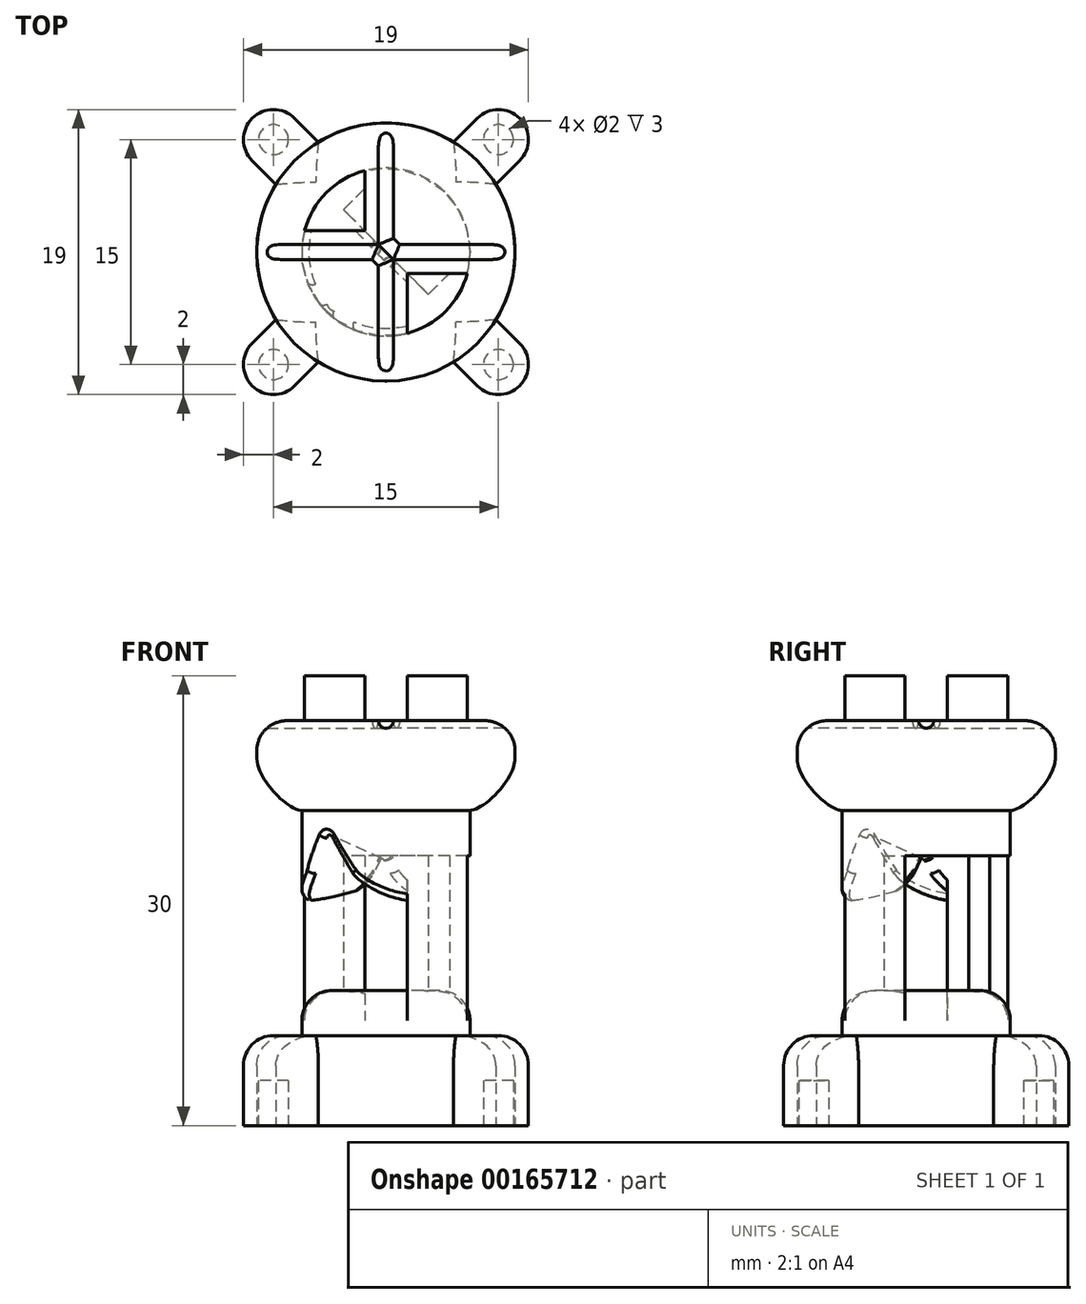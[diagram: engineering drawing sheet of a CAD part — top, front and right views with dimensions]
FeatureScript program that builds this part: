
annotation { "Feature Type Name" : "Feature", "Feature Type Description" : "" }
export const myFeature = defineFeature(function(context is Context, id is Id, definition is map)
    precondition{}
    {
        {
            assignVariable(context, id + "F0", {"name" : "squareSize", "anyValue" : 25 * mm});
        }
        {
            assignVariable(context, id + "F1", {"name" : "magnetHeight", "anyValue" : 3 * mm});
        }
        {
            assignVariable(context, id + "F2", {"name" : "thickness", "anyValue" : 3 * mm});
        }
        {
            var Q0;
            Q0=qCreatedBy(makeId("Top.planeOp"),FACE);
            var sketch = newSketch(context, id + "F3", { "sketchPlane" : qUnion([Q0])});
            skLineSegment(sketch, "E0.bottom", {"start": v(0, 0) * mm, "end": v(25, 0) * mm});
            skLineSegment(sketch, "E0.top", {"start": v(0, 25) * mm, "end": v(25, 25) * mm});
            skLineSegment(sketch, "E0.left", {"start": v(0, 0) * mm, "end": v(0, 25) * mm});
            skLineSegment(sketch, "E0.right", {"start": v(25, 0) * mm, "end": v(25, 25) * mm});
            skLineSegment(sketch, "E1", {"start": v(0, 0) * mm, "end": v(5, 0) * mm, "construction": true});
            skLineSegment(sketch, "E2", {"start": v(5, 0) * mm, "end": v(20, 0) * mm, "construction": true});
            skLineSegment(sketch, "E3", {"start": v(20, 0) * mm, "end": v(25, 0) * mm, "construction": true});
            skLineSegment(sketch, "E4", {"start": v(0, 0) * mm, "end": v(0, 5) * mm, "construction": true});
            skLineSegment(sketch, "E5", {"start": v(0, 5) * mm, "end": v(0, 20) * mm, "construction": true});
            skLineSegment(sketch, "E6", {"start": v(0, 20) * mm, "end": v(0, 25) * mm, "construction": true});
            skPoint(sketch, "E7", {"position": v(5, 5) * mm});
            skPoint(sketch, "E8", {"position": v(20, 5) * mm});
            skPoint(sketch, "E9", {"position": v(5, 20) * mm});
            skPoint(sketch, "E10", {"position": v(20, 20) * mm});
            skCircle(sketch, "E11", {"center": v(5, 20) * mm, "radius": 1 * mm});
            skCircle(sketch, "E12", {"center": v(20, 20) * mm, "radius": 1 * mm});
            skCircle(sketch, "E13", {"center": v(20, 5) * mm, "radius": 1 * mm});
            skCircle(sketch, "E14", {"center": v(5, 5) * mm, "radius": 1 * mm});
            skCircle(sketch, "E15", {"center": v(5, 20) * mm, "radius": 2 * mm});
            skCircle(sketch, "E16", {"center": v(20, 20) * mm, "radius": 2 * mm});
            skCircle(sketch, "E17", {"center": v(20, 5) * mm, "radius": 2 * mm});
            skCircle(sketch, "E18", {"center": v(5, 5) * mm, "radius": 2 * mm});
            skLineSegment(sketch, "E19", {"start": v(3.59, 18.59) * mm, "end": v(18.59, 3.59) * mm, "construction": true});
            skLineSegment(sketch, "E20", {"start": v(21.41, 6.41) * mm, "end": v(6.41, 21.41) * mm, "construction": true});
            skLineSegment(sketch, "E21", {"start": v(18.59, 21.41) * mm, "end": v(3.59, 6.41) * mm, "construction": true});
            skLineSegment(sketch, "E22", {"start": v(6.41, 3.59) * mm, "end": v(21.41, 18.59) * mm, "construction": true});
            skCircle(sketch, "E23", {"center": v(12.5, 12.5) * mm, "radius": 8.6 * mm});
            skPoint(sketch, "E23.centerSnap0", {"position": v(12.5, 0) * mm});
            skPoint(sketch, "E23.centerSnap1", {"position": v(0, 12.5) * mm});
            skLineSegment(sketch, "E24", {"start": v(18.59, 21.41) * mm, "end": v(17, 19.83) * mm});
            skLineSegment(sketch, "E25", {"start": v(21.41, 18.59) * mm, "end": v(19.83, 17) * mm});
            skLineSegment(sketch, "E26", {"start": v(21.41, 6.41) * mm, "end": v(19.83, 8) * mm});
            skLineSegment(sketch, "E27", {"start": v(18.59, 3.59) * mm, "end": v(17, 5.17) * mm});
            skLineSegment(sketch, "E28", {"start": v(3.59, 6.41) * mm, "end": v(5.17, 8) * mm});
            skLineSegment(sketch, "E29", {"start": v(6.41, 3.59) * mm, "end": v(8, 5.17) * mm});
            skLineSegment(sketch, "E30", {"start": v(3.59, 18.59) * mm, "end": v(5.17, 17) * mm});
            skLineSegment(sketch, "E31", {"start": v(6.41, 21.41) * mm, "end": v(8, 19.83) * mm});
            skCircle(sketch, "E32.0", {"center": v(12.5, 12.5) * mm, "radius": 5.6 * mm});
            skLineSegment(sketch, "E33", {"start": v(11.09, 13.91) * mm, "end": v(7.07, 13.91) * mm});
            skLineSegment(sketch, "E34", {"start": v(13.91, 11.09) * mm, "end": v(13.91, 7.07) * mm});
            skLineSegment(sketch, "E35", {"start": v(5, 20) * mm, "end": v(20, 5) * mm, "construction": true});
            skLineSegment(sketch, "E36", {"start": v(11.09, 17.93) * mm, "end": v(11.09, 16.74) * mm});
            skLineSegment(sketch, "E37", {"start": v(11.09, 16.74) * mm, "end": v(9.67, 15.33) * mm});
            skLineSegment(sketch, "E38", {"start": v(17.93, 11.09) * mm, "end": v(16.74, 11.09) * mm});
            skLineSegment(sketch, "E39", {"start": v(16.74, 11.09) * mm, "end": v(15.33, 9.67) * mm});
            skLineSegment(sketch, "E40", {"start": v(15.33, 9.67) * mm, "end": v(13.91, 11.09) * mm});
            skLineSegment(sketch, "E41", {"start": v(13.91, 11.09) * mm, "end": v(11.09, 13.91) * mm});
            skLineSegment(sketch, "E42", {"start": v(9.67, 15.33) * mm, "end": v(11.09, 13.91) * mm});
            skLineSegment(sketch, "E43", {"start": v(11.09, 13.91) * mm, "end": v(11.09, 16.74) * mm});
            skLineSegment(sketch, "E44", {"start": v(13.91, 11.09) * mm, "end": v(16.74, 11.09) * mm});
            skSolve(sketch);
        }
        {
            var Q0;
            Q0=makeQuery(id+"F3.imprint","IMPRINT",FACE,{"disambiguationData":[TD([[makeQuery(id+"F3.imprint","IMPRINT",EDGE,{"derivedFrom":sQuery(id+"F3.wireOp",EDGE,"E37")}),1.0]])]});
            var Q1;
            {var subQ1=sQuery(id+"F3.wireOp",EDGE,"E36");Q1=makeQuery(id+"F3.imprint","IMPRINT",FACE,{"disambiguationData":[TD([[makeQuery(id+"F3.imprint","IMPRINT",EDGE,{"derivedFrom":subQ1}),1.0]])]});}
            var Q2;
            {var subQ1=sQuery(id+"F3.wireOp",EDGE,"E33");Q2=makeQuery(id+"F3.imprint","IMPRINT",FACE,{"disambiguationData":[TD([[makeQuery(id+"F3.imprint","IMPRINT",EDGE,{"derivedFrom":subQ1}),-1.0]])]});}
            var Q3;
            {var subQ0=sQuery(id+"F3.wireOp",EDGE,"E34");Q3=makeQuery(id+"F3.imprint","IMPRINT",FACE,{"disambiguationData":[TD([[makeQuery(id+"F3.imprint","IMPRINT",EDGE,{"derivedFrom":subQ0}),1.0]])]});}
            var Q4;
            Q4=makeQuery(id+"F3.imprint","IMPRINT",FACE,{"disambiguationData":[TD([[makeQuery(id+"F3.imprint","IMPRINT",EDGE,{"derivedFrom":sQuery(id+"F3.wireOp",EDGE,"E39")}),-1.0]])]});
            var Q5;
            {var subQ0=sQuery(id+"F3.wireOp",EDGE,"E33");Q5=makeQuery(id+"F3.imprint","IMPRINT",FACE,{"disambiguationData":[TD([[makeQuery(id+"F3.imprint","IMPRINT",EDGE,{"derivedFrom":subQ0}),1.0]])]});}
            var Q6;
            {var subQ0=sQuery(id+"F3.wireOp",EDGE,"E23");var subQ11=makeQuery(id+"F3.imprint","INTERSECT",VERTEX,{"derivedFrom":[subQ0,sQuery(id+"F3.wireOp",EDGE,"E25")]});Q6=makeQuery(id+"F3.imprint","IMPRINT",FACE,{"disambiguationData":[TD([[makeQuery(id+"F3.imprint","IMPRINT",EDGE,{"disambiguationData":[TD([[subQ11,-1.0]])],"derivedFrom":subQ0}),1.0]])]});}
            var Q7;
            {var subQ0=sQuery(id+"F3.wireOp",EDGE,"E25");Q7=makeQuery(id+"F3.imprint","IMPRINT",FACE,{"disambiguationData":[TD([[makeQuery(id+"F3.imprint","IMPRINT",EDGE,{"derivedFrom":subQ0}),-1.0]])]});}
            var Q8;
            Q8=makeQuery(id+"F3.imprint","IMPRINT",FACE,{"disambiguationData":[TD([[makeQuery(id+"F3.imprint","IMPRINT",EDGE,{"derivedFrom":sQuery(id+"F3.wireOp",EDGE,"E12")}),-1.0]])]});
            var Q9;
            {var subQ0=sQuery(id+"F3.wireOp",EDGE,"E24");Q9=makeQuery(id+"F3.imprint","IMPRINT",FACE,{"disambiguationData":[TD([[makeQuery(id+"F3.imprint","IMPRINT",EDGE,{"derivedFrom":subQ0}),1.0]])]});}
            var Q10;
            {var subQ0=sQuery(id+"F3.wireOp",EDGE,"E30");Q10=makeQuery(id+"F3.imprint","IMPRINT",FACE,{"disambiguationData":[TD([[makeQuery(id+"F3.imprint","IMPRINT",EDGE,{"derivedFrom":subQ0}),1.0]])]});}
            var Q11;
            Q11=makeQuery(id+"F3.imprint","IMPRINT",FACE,{"disambiguationData":[TD([[makeQuery(id+"F3.imprint","IMPRINT",EDGE,{"derivedFrom":sQuery(id+"F3.wireOp",EDGE,"E11")}),-1.0]])]});
            var Q12;
            {var subQ0=sQuery(id+"F3.wireOp",EDGE,"E31");Q12=makeQuery(id+"F3.imprint","IMPRINT",FACE,{"disambiguationData":[TD([[makeQuery(id+"F3.imprint","IMPRINT",EDGE,{"derivedFrom":subQ0}),-1.0]])]});}
            var Q13;
            Q13=makeQuery(id+"F3.imprint","IMPRINT",FACE,{"disambiguationData":[TD([[makeQuery(id+"F3.imprint","IMPRINT",EDGE,{"derivedFrom":sQuery(id+"F3.wireOp",EDGE,"E14")}),-1.0]])]});
            var Q14;
            {var subQ0=sQuery(id+"F3.wireOp",EDGE,"E28");Q14=makeQuery(id+"F3.imprint","IMPRINT",FACE,{"disambiguationData":[TD([[makeQuery(id+"F3.imprint","IMPRINT",EDGE,{"derivedFrom":subQ0}),-1.0]])]});}
            var Q15;
            {var subQ0=sQuery(id+"F3.wireOp",EDGE,"E29");Q15=makeQuery(id+"F3.imprint","IMPRINT",FACE,{"disambiguationData":[TD([[makeQuery(id+"F3.imprint","IMPRINT",EDGE,{"derivedFrom":subQ0}),1.0]])]});}
            var Q16;
            {var subQ0=sQuery(id+"F3.wireOp",EDGE,"E27");Q16=makeQuery(id+"F3.imprint","IMPRINT",FACE,{"disambiguationData":[TD([[makeQuery(id+"F3.imprint","IMPRINT",EDGE,{"derivedFrom":subQ0}),-1.0]])]});}
            var Q17;
            Q17=makeQuery(id+"F3.imprint","IMPRINT",FACE,{"disambiguationData":[TD([[makeQuery(id+"F3.imprint","IMPRINT",EDGE,{"derivedFrom":sQuery(id+"F3.wireOp",EDGE,"E13")}),-1.0]])]});
            var Q18;
            {var subQ0=sQuery(id+"F3.wireOp",EDGE,"E26");Q18=makeQuery(id+"F3.imprint","IMPRINT",FACE,{"disambiguationData":[TD([[makeQuery(id+"F3.imprint","IMPRINT",EDGE,{"derivedFrom":subQ0}),1.0]])]});}
            var Q19;
            Q19=makeQuery(id+"FElZrmsSUFFGGNs_0.opExtrude","SWEPT_FACE",FACE,{"disambiguationData":[OSD([sQuery(id+"FqHbGi2moSqKO1t.wireOp",EDGE,"XD9OQdDl-AIoh-yf8k-eY9A-MIdfoNcweXZ7")])]});
            extrude(context, id + "F4", {"entities" : qUnion([Q0, Q1, Q2, Q3, Q4, Q5, Q6, Q7, Q8, Q9, Q10, Q11, Q12, Q13, Q14, Q15, Q16, Q17, Q18]), "endBoundEntityFace" : qUnion([Q19]), "depth" : getVariable(context, 'magnetHeight')});
        }
        {
            var Q0;
            Q0=makeQuery(id+"F4.opExtrude","CAP_FACE",FACE,{"disambiguationData":[OSD([sQuery(id+"F3.wireOp",EDGE,"E11"),sQuery(id+"F3.wireOp",EDGE,"E12"),sQuery(id+"F3.wireOp",EDGE,"E13"),sQuery(id+"F3.wireOp",EDGE,"E14"),sQuery(id+"F3.wireOp",EDGE,"E15"),sQuery(id+"F3.wireOp",EDGE,"E16"),sQuery(id+"F3.wireOp",EDGE,"E17"),sQuery(id+"F3.wireOp",EDGE,"E18"),sQuery(id+"F3.wireOp",EDGE,"E23"),sQuery(id+"F3.wireOp",EDGE,"E24"),sQuery(id+"F3.wireOp",EDGE,"E25"),sQuery(id+"F3.wireOp",EDGE,"E26"),sQuery(id+"F3.wireOp",EDGE,"E27"),sQuery(id+"F3.wireOp",EDGE,"E28"),sQuery(id+"F3.wireOp",EDGE,"E29"),sQuery(id+"F3.wireOp",EDGE,"E30"),sQuery(id+"F3.wireOp",EDGE,"E31")])],"isStart":false});
            var sketch = newSketch(context, id + "F5", { "sketchPlane" : qUnion([Q0])});
            skLineSegment(sketch, "E45.0", {"start": v(3.59, 18.59) * mm, "end": v(5.17, 17) * mm});
            skCircle(sketch, "E45.1", {"center": v(12.5, 12.5) * mm, "radius": 8.6 * mm});
            skCircle(sketch, "E45.2", {"center": v(5, 20) * mm, "radius": 2 * mm});
            skLineSegment(sketch, "E45.3", {"start": v(6.41, 21.41) * mm, "end": v(8, 19.83) * mm});
            skLineSegment(sketch, "E45.4", {"start": v(18.59, 21.41) * mm, "end": v(17, 19.83) * mm});
            skCircle(sketch, "E45.5", {"center": v(20, 20) * mm, "radius": 2 * mm});
            skLineSegment(sketch, "E45.6", {"start": v(21.41, 18.59) * mm, "end": v(19.83, 17) * mm});
            skLineSegment(sketch, "E45.7", {"start": v(21.41, 6.41) * mm, "end": v(19.83, 8) * mm});
            skCircle(sketch, "E46.0", {"center": v(20, 5) * mm, "radius": 2 * mm});
            skLineSegment(sketch, "E46.1", {"start": v(18.59, 3.59) * mm, "end": v(17, 5.17) * mm});
            skLineSegment(sketch, "E46.2", {"start": v(6.41, 3.59) * mm, "end": v(8, 5.17) * mm});
            skCircle(sketch, "E46.3", {"center": v(5, 5) * mm, "radius": 2 * mm});
            skLineSegment(sketch, "E47.0", {"start": v(3.59, 6.41) * mm, "end": v(5.17, 8) * mm});
            skSolve(sketch);
        }
        {
            var Q0;
            Q0 = qSketchRegion(id + "F5", true);
            var Q1;
            Q1=makeQuery(id+"FElZrmsSUFFGGNs_0.opExtrude","SWEPT_FACE",FACE,{"disambiguationData":[OSD([sQuery(id+"FqHbGi2moSqKO1t.wireOp",EDGE,"9eabc2cb-ff13-4b68-a3ec-a71c30de9d8a")])]});
            var Q2;
            Q2=makeQuery(id+"FElZrmsSUFFGGNs_0.opExtrude","SWEPT_FACE",FACE,{"disambiguationData":[OSD([sQuery(id+"FqHbGi2moSqKO1t.wireOp",EDGE,"XD9OQdDl-AIoh-yf8k-eY9A-MIdfoNcweXZ7")])]});
            extrude(context, id + "F6", {"entities" : qUnion([Q0]), "operationType" : NewBodyOperationType.ADD, "endBoundEntityFace" : qUnion([Q1]), "depth" : getVariable(context, 'thickness')});
        }
        {
            var Q0;
            Q0=makeQuery(id+"F6.opExtrude","CAP_FACE",FACE,{"disambiguationData":[OSD([sQuery(id+"F5.wireOp",EDGE,"E45.0"),sQuery(id+"F5.wireOp",EDGE,"E45.1"),sQuery(id+"F5.wireOp",EDGE,"E45.2"),sQuery(id+"F5.wireOp",EDGE,"E45.3"),sQuery(id+"F5.wireOp",EDGE,"E45.4"),sQuery(id+"F5.wireOp",EDGE,"E45.5"),sQuery(id+"F5.wireOp",EDGE,"E45.6"),sQuery(id+"F5.wireOp",EDGE,"E45.7"),sQuery(id+"F5.wireOp",EDGE,"E46.0"),sQuery(id+"F5.wireOp",EDGE,"E46.1"),sQuery(id+"F5.wireOp",EDGE,"E46.2"),sQuery(id+"F5.wireOp",EDGE,"E46.3"),sQuery(id+"F5.wireOp",EDGE,"E47.0")])],"isStart":false});
            var sketch = newSketch(context, id + "F7", { "sketchPlane" : qUnion([Q0])});
            skCircle(sketch, "E48.0", {"center": v(12.5, 12.5) * mm, "radius": 5.6 * mm});
            skSolve(sketch);
        }
        {
            var Q0;
            Q0 = qSketchRegion(id + "F7", true);
            var Q1;
            Q1=makeQuery(id+"FElZrmsSUFFGGNs_0.opExtrude","SWEPT_FACE",FACE,{"disambiguationData":[OSD([sQuery(id+"FqHbGi2moSqKO1t.wireOp",EDGE,"AaM88Yrc-j56C-Fqkk-HDkq-REDH0FS8FcKS")])]});
            var Q2;
            Q2=makeQuery(id+"FElZrmsSUFFGGNs_0.opExtrude","SWEPT_FACE",FACE,{"disambiguationData":[OSD([sQuery(id+"FqHbGi2moSqKO1t.wireOp",EDGE,"9eabc2cb-ff13-4b68-a3ec-a71c30de9d8a")])]});
            extrude(context, id + "F8", {"entities" : qUnion([Q0]), "operationType" : NewBodyOperationType.ADD, "endBoundEntityFace" : qUnion([Q1]), "depth" : getVariable(context, 'thickness')});
        }
        {
            var Q0;
            Q0=makeQuery(id+"F8.opExtrude","CAP_FACE",FACE,{"disambiguationData":[OSD([sQuery(id+"F7.wireOp",EDGE,"E48.0")])],"isStart":false});
            var sketch = newSketch(context, id + "F9", { "sketchPlane" : qUnion([Q0])});
            skLineSegment(sketch, "E49.0", {"start": v(11.09, 13.91) * mm, "end": v(7.07, 13.91) * mm});
            skLineSegment(sketch, "E49.1", {"start": v(9.67, 15.33) * mm, "end": v(11.09, 13.91) * mm});
            skLineSegment(sketch, "E49.2", {"start": v(11.09, 16.74) * mm, "end": v(9.67, 15.33) * mm});
            skCircle(sketch, "E49.3", {"center": v(12.5, 12.5) * mm, "radius": 5.6 * mm});
            skLineSegment(sketch, "E49.4", {"start": v(15.33, 9.67) * mm, "end": v(13.91, 11.09) * mm});
            skLineSegment(sketch, "E49.5", {"start": v(16.74, 11.09) * mm, "end": v(15.33, 9.67) * mm});
            skLineSegment(sketch, "E49.6", {"start": v(17.93, 11.09) * mm, "end": v(16.74, 11.09) * mm});
            skLineSegment(sketch, "E49.7", {"start": v(11.09, 17.93) * mm, "end": v(11.09, 16.74) * mm});
            skLineSegment(sketch, "E49.8", {"start": v(13.91, 11.09) * mm, "end": v(13.91, 7.07) * mm});
            skSolve(sketch);
        }
        {
            var Q0;
            {var subQ1=sQuery(id+"F9.wireOp",EDGE,"E49.0");Q0=makeQuery(id+"F9.imprint","IMPRINT",FACE,{"disambiguationData":[TD([[makeQuery(id+"F9.imprint","IMPRINT",EDGE,{"derivedFrom":subQ1}),-1.0]])]});}
            var Q1;
            Q1=makeQuery(id+"F9.imprint","IMPRINT",FACE,{"disambiguationData":[TD([[makeQuery(id+"F9.imprint","IMPRINT",EDGE,{"derivedFrom":sQuery(id+"F9.wireOp",EDGE,"E49.4")}),1.0]])]});
            var Q2;
            Q2=makeQuery(id+"FElZrmsSUFFGGNs_0.opExtrude","SWEPT_FACE",FACE,{"disambiguationData":[OSD([sQuery(id+"FqHbGi2moSqKO1t.wireOp",EDGE,"z7yksMqY-2ZQH-XZhy-clyX-XMTxwlro2wc1")])]});
            var Q3;
            Q3=makeQuery(id+"FElZrmsSUFFGGNs_0.opExtrude","SWEPT_FACE",FACE,{"disambiguationData":[OSD([sQuery(id+"FqHbGi2moSqKO1t.wireOp",EDGE,"AaM88Yrc-j56C-Fqkk-HDkq-REDH0FS8FcKS")])]});
            extrude(context, id + "F10", {"entities" : qUnion([Q0, Q1]), "operationType" : NewBodyOperationType.ADD, "endBoundEntityFace" : qUnion([Q2]), "depth" : 2 * getVariable(context, 'thickness')});
        }
        {
            var Q0;
            Q0=makeQuery(id+"F10.opExtrude","CAP_FACE",FACE,{"disambiguationData":[OSD([sQuery(id+"F9.wireOp",EDGE,"E49.3"),sQuery(id+"F9.wireOp",EDGE,"E49.4"),sQuery(id+"F9.wireOp",EDGE,"E49.5"),sQuery(id+"F9.wireOp",EDGE,"E49.6"),sQuery(id+"F9.wireOp",EDGE,"E49.8")])],"isStart":false});
            var sketch = newSketch(context, id + "F11", { "sketchPlane" : qUnion([Q0])});
            skLineSegment(sketch, "E50.0", {"start": v(15.33, 9.67) * mm, "end": v(13.91, 11.09) * mm});
            skLineSegment(sketch, "E50.1", {"start": v(16.74, 11.09) * mm, "end": v(15.33, 9.67) * mm});
            skLineSegment(sketch, "E50.2", {"start": v(17.93, 11.09) * mm, "end": v(16.74, 11.09) * mm});
            skCircle(sketch, "E50.3", {"center": v(12.5, 12.5) * mm, "radius": 5.6 * mm});
            skLineSegment(sketch, "E51.0", {"start": v(9.67, 15.33) * mm, "end": v(11.09, 13.91) * mm});
            skLineSegment(sketch, "E51.1", {"start": v(11.09, 16.74) * mm, "end": v(9.67, 15.33) * mm});
            skLineSegment(sketch, "E51.2", {"start": v(11.09, 17.93) * mm, "end": v(11.09, 16.74) * mm});
            skLineSegment(sketch, "E52", {"start": v(11.09, 13.91) * mm, "end": v(13.91, 11.09) * mm});
            skSolve(sketch);
        }
        {
            var Q0;
            Q0=makeQuery(id+"F11.imprint","IMPRINT",FACE,{"disambiguationData":[TD([[makeQuery(id+"F11.imprint","IMPRINT",EDGE,{"derivedFrom":sQuery(id+"F11.wireOp",EDGE,"E50.0")}),1.0]])]});
            var Q1;
            Q1=makeQuery(id+"F11.imprint","IMPRINT",FACE,{"disambiguationData":[TD([[makeQuery(id+"F11.imprint","IMPRINT",EDGE,{"derivedFrom":sQuery(id+"F11.wireOp",EDGE,"E51.0")}),-1.0]])]});
            extrude(context, id + "F12", {"entities" : qUnion([Q0, Q1]), "operationType" : NewBodyOperationType.ADD, "depth" : getVariable(context, 'thickness')});
        }
        {
            var Q0;
            Q0=makeQuery(id+"F12.opExtrude","CAP_FACE",FACE,{"disambiguationData":[OSD([sQuery(id+"F11.wireOp",EDGE,"E50.0"),sQuery(id+"F11.wireOp",EDGE,"E50.1"),sQuery(id+"F11.wireOp",EDGE,"E50.2"),sQuery(id+"F11.wireOp",EDGE,"E50.3"),sQuery(id+"F11.wireOp",EDGE,"E51.0"),sQuery(id+"F11.wireOp",EDGE,"E51.1"),sQuery(id+"F11.wireOp",EDGE,"E51.2"),sQuery(id+"F11.wireOp",EDGE,"E52")])],"isStart":false});
            var sketch = newSketch(context, id + "F13", { "sketchPlane" : qUnion([Q0])});
            skCircle(sketch, "E53.0", {"center": v(12.5, 12.5) * mm, "radius": 5.6 * mm});
            skSolve(sketch);
        }
        {
            var Q0;
            Q0=makeQuery(id+"F13.imprint","IMPRINT",FACE,{"disambiguationData":[TD([[makeQuery(id+"F13.imprint","IMPRINT",EDGE,{"derivedFrom":makeQuery(id+"F12.opExtrude","CAP_EDGE",EDGE,{"disambiguationData":[OSD([sQuery(id+"F11.wireOp",EDGE,"E50.1")])],"isStart":false})}),1.0]])]});
            var Q1;
            Q1=makeQuery(id+"F13.imprint","IMPRINT",FACE,{"disambiguationData":[TD([[makeQuery(id+"F13.imprint","IMPRINT",EDGE,{"derivedFrom":makeQuery(id+"F12.opExtrude","CAP_EDGE",EDGE,{"disambiguationData":[OSD([sQuery(id+"F11.wireOp",EDGE,"E50.1")])],"isStart":false})}),-1.0]])]});
            var Q2;
            Q2=makeQuery(id+"FElZrmsSUFFGGNs_0.opExtrude","SWEPT_FACE",FACE,{"disambiguationData":[OSD([sQuery(id+"FqHbGi2moSqKO1t.wireOp",EDGE,"eM3HZQxG-NVRT-AnBt-5DXk-xiImXyo5NWNo")])]});
            var Q3;
            Q3=makeQuery(id+"FElZrmsSUFFGGNs_0.opExtrude","SWEPT_FACE",FACE,{"disambiguationData":[OSD([sQuery(id+"FqHbGi2moSqKO1t.wireOp",EDGE,"z7yksMqY-2ZQH-XZhy-clyX-XMTxwlro2wc1")])]});
            extrude(context, id + "F14", {"entities" : qUnion([Q0, Q1]), "operationType" : NewBodyOperationType.ADD, "endBoundEntityFace" : qUnion([Q2]), "depth" : getVariable(context, 'thickness')});
        }
        {
            var Q0;
            Q0=makeQuery(id+"F14.opExtrude","CAP_FACE",FACE,{"disambiguationData":[OSD([sQuery(id+"F13.wireOp",EDGE,"E53.0")])],"isStart":false});
            var sketch = newSketch(context, id + "F15", { "sketchPlane" : qUnion([Q0])});
            skCircle(sketch, "E54.0", {"center": v(12.5, 12.5) * mm, "radius": 8.6 * mm});
            skSolve(sketch);
        }
        {
            var Q0;
            Q0 = qSketchRegion(id + "F15", true);
            var Q1;
            Q1=makeQuery(id+"FElZrmsSUFFGGNs_0.opExtrude","SWEPT_FACE",FACE,{"disambiguationData":[OSD([sQuery(id+"FqHbGi2moSqKO1t.wireOp",EDGE,"O0l0VlI1-JJUv-K6Yr-c7LZ-AkOMDPOYUOIM")])]});
            var Q2;
            Q2=makeQuery(id+"FElZrmsSUFFGGNs_0.opExtrude","SWEPT_FACE",FACE,{"disambiguationData":[OSD([sQuery(id+"FqHbGi2moSqKO1t.wireOp",EDGE,"eM3HZQxG-NVRT-AnBt-5DXk-xiImXyo5NWNo")])]});
            extrude(context, id + "F16", {"entities" : qUnion([Q0]), "operationType" : NewBodyOperationType.ADD, "endBoundEntityFace" : qUnion([Q1]), "depth" : 2 * getVariable(context, 'thickness')});
        }
        {
            var Q0;
            Q0=makeQuery(id+"F16.opExtrude","CAP_FACE",FACE,{"disambiguationData":[OSD([sQuery(id+"F15.wireOp",EDGE,"E54.0")])],"isStart":false});
            var sketch = newSketch(context, id + "F17", { "sketchPlane" : qUnion([Q0])});
            skLineSegment(sketch, "E55.0", {"start": v(11.09, 13.91) * mm, "end": v(7.07, 13.91) * mm});
            skCircle(sketch, "E55.1", {"center": v(12.5, 12.5) * mm, "radius": 5.6 * mm});
            skLineSegment(sketch, "E55.4", {"start": v(11.09, 17.93) * mm, "end": v(11.09, 16.74) * mm});
            skLineSegment(sketch, "E55.5", {"start": v(13.91, 11.09) * mm, "end": v(13.91, 7.07) * mm});
            skLineSegment(sketch, "E55.8", {"start": v(17.93, 11.09) * mm, "end": v(16.74, 11.09) * mm});
            skLineSegment(sketch, "E56.0", {"start": v(13.91, 11.09) * mm, "end": v(16.74, 11.09) * mm});
            skLineSegment(sketch, "E56.1", {"start": v(11.09, 13.91) * mm, "end": v(11.09, 16.74) * mm});
            skSolve(sketch);
        }
        {
            var Q0;
            {var subQ0=sQuery(id+"F17.wireOp",EDGE,"E55.0");Q0=makeQuery(id+"F17.imprint","IMPRINT",FACE,{"disambiguationData":[TD([[makeQuery(id+"F17.imprint","IMPRINT",EDGE,{"derivedFrom":subQ0}),-1.0]])]});}
            var Q1;
            {var subQ0=sQuery(id+"F17.wireOp",EDGE,"E55.5");Q1=makeQuery(id+"F17.imprint","IMPRINT",FACE,{"disambiguationData":[TD([[makeQuery(id+"F17.imprint","IMPRINT",EDGE,{"derivedFrom":subQ0}),1.0]])]});}
            var Q2;
            Q2=makeQuery(id+"FElZrmsSUFFGGNs_0.opExtrude","SWEPT_FACE",FACE,{"disambiguationData":[OSD([sQuery(id+"FqHbGi2moSqKO1t.wireOp",EDGE,"O0l0VlI1-JJUv-K6Yr-c7LZ-AkOMDPOYUOIM")])]});
            extrude(context, id + "F18", {"entities" : qUnion([Q0, Q1]), "operationType" : NewBodyOperationType.ADD, "depth" : getVariable(context, 'thickness')});
        }
        {
            var Q0;
            Q0=makeQuery(id+"F12.boolean.opBoolean","MERGE",FACE,{"derivedFrom":[makeQuery(id+"F10.opExtrude","SWEPT_FACE",FACE,{"disambiguationData":[OSD([sQuery(id+"F9.wireOp",EDGE,"E49.1")])]}),makeQuery(id+"F10.opExtrude","SWEPT_FACE",FACE,{"disambiguationData":[OSD([sQuery(id+"F9.wireOp",EDGE,"E49.4")])]}),makeQuery(id+"F12.opExtrude","SWEPT_FACE",FACE,{"disambiguationData":[OSD([sQuery(id+"F11.wireOp",EDGE,"E50.0"),sQuery(id+"F11.wireOp",EDGE,"E51.0"),sQuery(id+"F11.wireOp",EDGE,"E52")])]})]});
            var sketch = newSketch(context, id + "F19", { "sketchPlane" : qUnion([Q0])});
            skLineSegment(sketch, "E57.0", {"start": v(-2, 15) * mm, "end": v(2, 15) * mm});
            skLineSegment(sketch, "E57.1", {"start": v(-4, 18) * mm, "end": v(4, 18) * mm});
            skLineSegment(sketch, "E58", {"start": v(2, 15) * mm, "end": v(0, 18) * mm});
            skLineSegment(sketch, "E59", {"start": v(-2, 15) * mm, "end": v(0, 18) * mm});
            skSolve(sketch);
        }
        {
            var Q0;
            Q0=makeQuery(id+"F19.imprint","IMPRINT",FACE,{"disambiguationData":[TD([[makeQuery(id+"F19.imprint","IMPRINT",EDGE,{"derivedFrom":sQuery(id+"F19.wireOp",EDGE,"E57.0")}),1.0]])]});
            extrude(context, id + "F20", {"entities" : qUnion([Q0]), "operationType" : NewBodyOperationType.REMOVE, "oppositeDirection" : true, "depth" : 25 * mm, "hasDraft" : true, "draftAngle" : 10 * degree});
        }
        {
            var Q0;
            Q0=makeQuery(id+"F20.boolean.opBoolean","INTERSECT",EDGE,{"derivedFrom":[makeQuery(id+"F12.opExtrude","CAP_FACE",FACE,{"disambiguationData":[OSD([sQuery(id+"F11.wireOp",EDGE,"E50.0"),sQuery(id+"F11.wireOp",EDGE,"E50.1"),sQuery(id+"F11.wireOp",EDGE,"E50.2"),sQuery(id+"F11.wireOp",EDGE,"E50.3"),sQuery(id+"F11.wireOp",EDGE,"E51.0"),sQuery(id+"F11.wireOp",EDGE,"E51.1"),sQuery(id+"F11.wireOp",EDGE,"E51.2"),sQuery(id+"F11.wireOp",EDGE,"E52")])],"isStart":true}),makeQuery(id+"F20.opExtrude","SWEPT_FACE",FACE,{"disambiguationData":[OSD([sQuery(id+"F19.wireOp",EDGE,"E58")])]})]});
            var Q1;
            Q1=makeQuery(id+"F20.boolean.opBoolean","INTERSECT",EDGE,{"derivedFrom":[makeQuery(id+"F12.opExtrude","CAP_FACE",FACE,{"disambiguationData":[OSD([sQuery(id+"F11.wireOp",EDGE,"E50.0"),sQuery(id+"F11.wireOp",EDGE,"E50.1"),sQuery(id+"F11.wireOp",EDGE,"E50.2"),sQuery(id+"F11.wireOp",EDGE,"E50.3"),sQuery(id+"F11.wireOp",EDGE,"E51.0"),sQuery(id+"F11.wireOp",EDGE,"E51.1"),sQuery(id+"F11.wireOp",EDGE,"E51.2"),sQuery(id+"F11.wireOp",EDGE,"E52")])],"isStart":true}),makeQuery(id+"F20.opExtrude","SWEPT_FACE",FACE,{"disambiguationData":[OSD([sQuery(id+"F19.wireOp",EDGE,"E59")])]})]});
            fillet(context, id + "F21", {"entities" : qUnion([Q0, Q1]), "radius" : 4 * mm, "tangentPropagation" : true, "rho" : 0.3, "crossSection" : FilletCrossSection.CONIC, "allowEdgeOverflow" : false});
        }
        {
            var Q0;
            Q0=makeQuery(id+"F20.boolean.opBoolean","COPY",FACE,{"derivedFrom":makeQuery(id+"F20.opExtrude","SWEPT_FACE",FACE,{"disambiguationData":[OSD([sQuery(id+"F19.wireOp",EDGE,"E59")])]})});
            var Q1;
            Q1=makeQuery(id+"F20.boolean.opBoolean","COPY",FACE,{"derivedFrom":makeQuery(id+"F20.opExtrude","SWEPT_FACE",FACE,{"disambiguationData":[OSD([sQuery(id+"F19.wireOp",EDGE,"E58")])]})});
            fillet(context, id + "F22", {"entities" : qUnion([Q0, Q1]), "radius" : 0.4 * mm, "tangentPropagation" : true, "allowEdgeOverflow" : false});
        }
        {
            var Q0;
            Q0=makeQuery(id+"F16.opExtrude","CAP_EDGE",EDGE,{"disambiguationData":[OSD([sQuery(id+"F15.wireOp",EDGE,"E54.0")])],"isStart":false});
            var Q1;
            {var subQ1=sQuery(id+"F9.wireOp",EDGE,"E49.0");var subQ2=sQuery(id+"F7.wireOp",EDGE,"E48.0");Q1=makeQuery(id+"F10.boolean.opBoolean","SPLIT",EDGE,{"disambiguationData":[TD([makeQuery(id+"F10.opExtrude","SWEPT_FACE",FACE,{"disambiguationData":[OSD([subQ1])]})])],"derivedFrom":makeQuery(id+"F8.opExtrude","CAP_EDGE",EDGE,{"disambiguationData":[OSD([subQ2])],"isStart":false})});}
            var Q2;
            {var subQ0=sQuery(id+"F5.wireOp",EDGE,"E45.1");Q2=makeQuery(id+"F6.opExtrude","CAP_EDGE",EDGE,{"disambiguationData":[OSD([subQ0]),TDD([makeQuery(id+"F5.imprint","IMPRINT",EDGE,{"disambiguationData":[TD([[makeQuery(id+"F5.imprint","INTERSECT",VERTEX,{"derivedFrom":[subQ0,sQuery(id+"F5.wireOp",EDGE,"E47.0")]}),1.0]])],"derivedFrom":subQ0})])],"isStart":false});}
            var Q3;
            Q3=makeQuery(id+"F6.opExtrude","CAP_EDGE",EDGE,{"disambiguationData":[OSD([sQuery(id+"F5.wireOp",EDGE,"E46.3")])],"isStart":false});
            var Q4;
            Q4=makeQuery(id+"F6.opExtrude","CAP_EDGE",EDGE,{"disambiguationData":[OSD([sQuery(id+"F5.wireOp",EDGE,"E47.0")])],"isStart":false});
            var Q5;
            Q5=makeQuery(id+"F6.opExtrude","CAP_EDGE",EDGE,{"disambiguationData":[OSD([sQuery(id+"F5.wireOp",EDGE,"E46.2")])],"isStart":false});
            var Q6;
            Q6=makeQuery(id+"F6.opExtrude","CAP_EDGE",EDGE,{"disambiguationData":[OSD([sQuery(id+"F5.wireOp",EDGE,"E46.1")])],"isStart":false});
            var Q7;
            Q7=makeQuery(id+"F6.opExtrude","CAP_EDGE",EDGE,{"disambiguationData":[OSD([sQuery(id+"F5.wireOp",EDGE,"E46.0")])],"isStart":false});
            var Q8;
            Q8=makeQuery(id+"F6.opExtrude","CAP_EDGE",EDGE,{"disambiguationData":[OSD([sQuery(id+"F5.wireOp",EDGE,"E45.7")])],"isStart":false});
            var Q9;
            {var subQ0=sQuery(id+"F5.wireOp",EDGE,"E45.1");Q9=makeQuery(id+"F6.opExtrude","CAP_EDGE",EDGE,{"disambiguationData":[OSD([subQ0]),TDD([makeQuery(id+"F5.imprint","IMPRINT",EDGE,{"disambiguationData":[TD([[makeQuery(id+"F5.imprint","INTERSECT",VERTEX,{"derivedFrom":[subQ0,sQuery(id+"F5.wireOp",EDGE,"E45.6")]}),1.0]])],"derivedFrom":subQ0})])],"isStart":false});}
            var Q10;
            {var subQ0=sQuery(id+"F5.wireOp",EDGE,"E45.1");Q10=makeQuery(id+"F6.opExtrude","CAP_EDGE",EDGE,{"disambiguationData":[OSD([subQ0]),TDD([makeQuery(id+"F5.imprint","IMPRINT",EDGE,{"disambiguationData":[TD([[makeQuery(id+"F5.imprint","INTERSECT",VERTEX,{"derivedFrom":[subQ0,sQuery(id+"F5.wireOp",EDGE,"E46.1")]}),1.0]])],"derivedFrom":subQ0})])],"isStart":false});}
            var Q11;
            Q11=makeQuery(id+"F6.opExtrude","CAP_EDGE",EDGE,{"disambiguationData":[OSD([sQuery(id+"F5.wireOp",EDGE,"E45.6")])],"isStart":false});
            var Q12;
            Q12=makeQuery(id+"F6.opExtrude","CAP_EDGE",EDGE,{"disambiguationData":[OSD([sQuery(id+"F5.wireOp",EDGE,"E45.5")])],"isStart":false});
            var Q13;
            Q13=makeQuery(id+"F6.opExtrude","CAP_EDGE",EDGE,{"disambiguationData":[OSD([sQuery(id+"F5.wireOp",EDGE,"E45.4")])],"isStart":false});
            var Q14;
            {var subQ0=sQuery(id+"F5.wireOp",EDGE,"E45.1");Q14=makeQuery(id+"F6.opExtrude","CAP_EDGE",EDGE,{"disambiguationData":[OSD([subQ0]),TDD([makeQuery(id+"F5.imprint","IMPRINT",EDGE,{"disambiguationData":[TD([[makeQuery(id+"F5.imprint","INTERSECT",VERTEX,{"derivedFrom":[subQ0,sQuery(id+"F5.wireOp",EDGE,"E45.4")]}),-1.0]])],"derivedFrom":subQ0})])],"isStart":false});}
            var Q15;
            Q15=makeQuery(id+"F6.opExtrude","CAP_EDGE",EDGE,{"disambiguationData":[OSD([sQuery(id+"F5.wireOp",EDGE,"E45.3")])],"isStart":false});
            var Q16;
            Q16=makeQuery(id+"F6.opExtrude","CAP_EDGE",EDGE,{"disambiguationData":[OSD([sQuery(id+"F5.wireOp",EDGE,"E45.2")])],"isStart":false});
            var Q17;
            Q17=makeQuery(id+"F6.opExtrude","CAP_EDGE",EDGE,{"disambiguationData":[OSD([sQuery(id+"F5.wireOp",EDGE,"E45.0")])],"isStart":false});
            var Q18;
            {var subQ0=sQuery(id+"F9.wireOp",EDGE,"E49.6");var subQ3=sQuery(id+"F7.wireOp",EDGE,"E48.0");Q18=makeQuery(id+"F10.boolean.opBoolean","SPLIT",EDGE,{"disambiguationData":[TD([makeQuery(id+"F10.opExtrude","SWEPT_FACE",FACE,{"disambiguationData":[OSD([subQ0])]})])],"derivedFrom":makeQuery(id+"F8.opExtrude","CAP_EDGE",EDGE,{"disambiguationData":[OSD([subQ3])],"isStart":false})});}
            fillet(context, id + "F23", {"entities" : qUnion([Q0, Q1, Q2, Q3, Q4, Q5, Q6, Q7, Q8, Q9, Q10, Q11, Q12, Q13, Q14, Q15, Q16, Q17, Q18]), "radius" : 2 * mm, "tangentPropagation" : true, "allowEdgeOverflow" : false});
        }
        {
            var Q0;
            Q0=qCreatedBy(makeId("Right.planeOp"),FACE);
            var sketch = newSketch(context, id + "F24", { "sketchPlane" : qUnion([Q0])});
            skLineSegment(sketch, "E60.0", {"start": v(13.91, 27) * mm, "end": v(17.93, 27) * mm, "construction": true});
            skLineSegment(sketch, "E60.1", {"start": v(11.09, 27) * mm, "end": v(7.07, 27) * mm, "construction": true});
            skLineSegment(sketch, "E61", {"start": v(13.91, 27) * mm, "end": v(11.09, 27) * mm, "construction": true});
            skCircle(sketch, "E62", {"center": v(12.5, 27) * mm, "radius": 0.5 * mm});
            skSolve(sketch);
        }
        {
            var Q0;
            Q0=makeQuery(id+"F16.opExtrude","CAP_FACE",FACE,{"disambiguationData":[OSD([sQuery(id+"F15.wireOp",EDGE,"E54.0")])],"isStart":false});
            var sketch = newSketch(context, id + "F25", { "sketchPlane" : qUnion([Q0])});
            skLineSegment(sketch, "E63.0", {"start": v(13.91, 11.09) * mm, "end": v(11.09, 13.91) * mm});
            skCircle(sketch, "E64.0", {"center": v(12.5, 12.5) * mm, "radius": 6.6 * mm});
            skLineSegment(sketch, "E65", {"start": v(12.5, 12.5) * mm, "end": v(0, 12.5) * mm, "construction": true});
            skLineSegment(sketch, "E66", {"start": v(12.5, 12.5) * mm, "end": v(12.5, 0) * mm, "construction": true});
            skLineSegment(sketch, "E67", {"start": v(12.5, 12.5) * mm, "end": v(25, 12.5) * mm, "construction": true});
            skLineSegment(sketch, "E68", {"start": v(12.5, 12.5) * mm, "end": v(12.5, 25) * mm, "construction": true});
            skLineSegment(sketch, "E69.0", {"start": v(13.2, 12.5) * mm, "end": v(12.5, 13.2) * mm});
            skLineSegment(sketch, "E70.0", {"start": v(12.5, 11.8) * mm, "end": v(11.8, 12.5) * mm});
            skLineSegment(sketch, "E71", {"start": v(0, 12.5) * mm, "end": v(11.8, 12.5) * mm});
            skLineSegment(sketch, "E72", {"start": v(12.5, 11.8) * mm, "end": v(12.5, 0) * mm});
            skLineSegment(sketch, "E73", {"start": v(25, 12.5) * mm, "end": v(13.2, 12.5) * mm});
            skLineSegment(sketch, "E74", {"start": v(12.5, 13.2) * mm, "end": v(12.5, 25) * mm});
            skSolve(sketch);
        }
        {
            var Q0;
            Q0=makeQuery(id+"F24.imprint","IMPRINT",FACE,{"disambiguationData":[TD([[makeQuery(id+"F24.imprint","IMPRINT",EDGE,{"derivedFrom":sQuery(id+"F24.wireOp",EDGE,"E62")}),1.0]])]});
            var Q1;
            Q1=sQuery(id+"F25.wireOp",EDGE,"E71");
            var Q2;
            Q2=sQuery(id+"F25.wireOp",EDGE,"E70.0");
            var Q3;
            Q3=sQuery(id+"F25.wireOp",EDGE,"E72");
            sweep(context, id + "F26", {"operationType" : NewBodyOperationType.REMOVE, "profiles" : qUnion([Q0]), "path" : qUnion([Q1, Q2, Q3])});
        }
        {
            var Q0;
            Q0=qCreatedBy(makeId("Right.planeOp"),FACE);
            cPlane(context, id + "F27", {"entities" : qUnion([Q0]), "cplaneType" : CPlaneType.OFFSET, "offset" : getVariable(context, 'squareSize'), "width" : 150 * mm, "height" : 150 * mm});
        }
        {
            var Q0;
            Q0=qCreatedBy(id+"F27.planeOp",FACE);
            var sketch = newSketch(context, id + "F28", { "sketchPlane" : qUnion([Q0])});
            skCircle(sketch, "E75.0", {"center": v(12.5, 27) * mm, "radius": 0.5 * mm});
            skSolve(sketch);
        }
        {
            var Q0;
            Q0 = qSketchRegion(id + "F28", true);
            var Q1;
            Q1=sQuery(id+"F25.wireOp",EDGE,"E73");
            var Q2;
            Q2=sQuery(id+"F25.wireOp",EDGE,"E69.0");
            var Q3;
            Q3=sQuery(id+"F25.wireOp",EDGE,"E74");
            sweep(context, id + "F29", {"operationType" : NewBodyOperationType.REMOVE, "profiles" : qUnion([Q0]), "path" : qUnion([Q1, Q2, Q3])});
        }
        {
            var Q0;
            {var subQ1=sQuery(id+"F9.wireOp",EDGE,"E49.0");var subQ2=sQuery(id+"F7Ht8o9fmuo8yMg_15.wireOp",EDGE,"3cd4ca64-c1fa-4839-9213-f8b566fa8048.0");Q0=makeQuery(id+"F14.boolean.opBoolean","SPLIT",EDGE,{"disambiguationData":[TD([makeQuery(id+"F10.opExtrude","SWEPT_FACE",FACE,{"disambiguationData":[OSD([subQ1])]})])],"derivedFrom":makeQuery(id+"F14.opExtrude","CAP_EDGE",EDGE,{"disambiguationData":[OSD([subQ2])],"isStart":true})});}
            var Q1;
            Q1=makeQuery(id+"F16.opExtrude","CAP_EDGE",EDGE,{"disambiguationData":[OSD([sQuery(id+"F15.wireOp",EDGE,"E54.0")])],"isStart":true});
            fillet(context, id + "F30", {"entities" : qUnion([Q0, Q1]), "radius" : 3.5 * mm, "tangentPropagation" : true, "rho" : 0.3, "crossSection" : FilletCrossSection.CONIC, "allowEdgeOverflow" : false});
        }
    });
